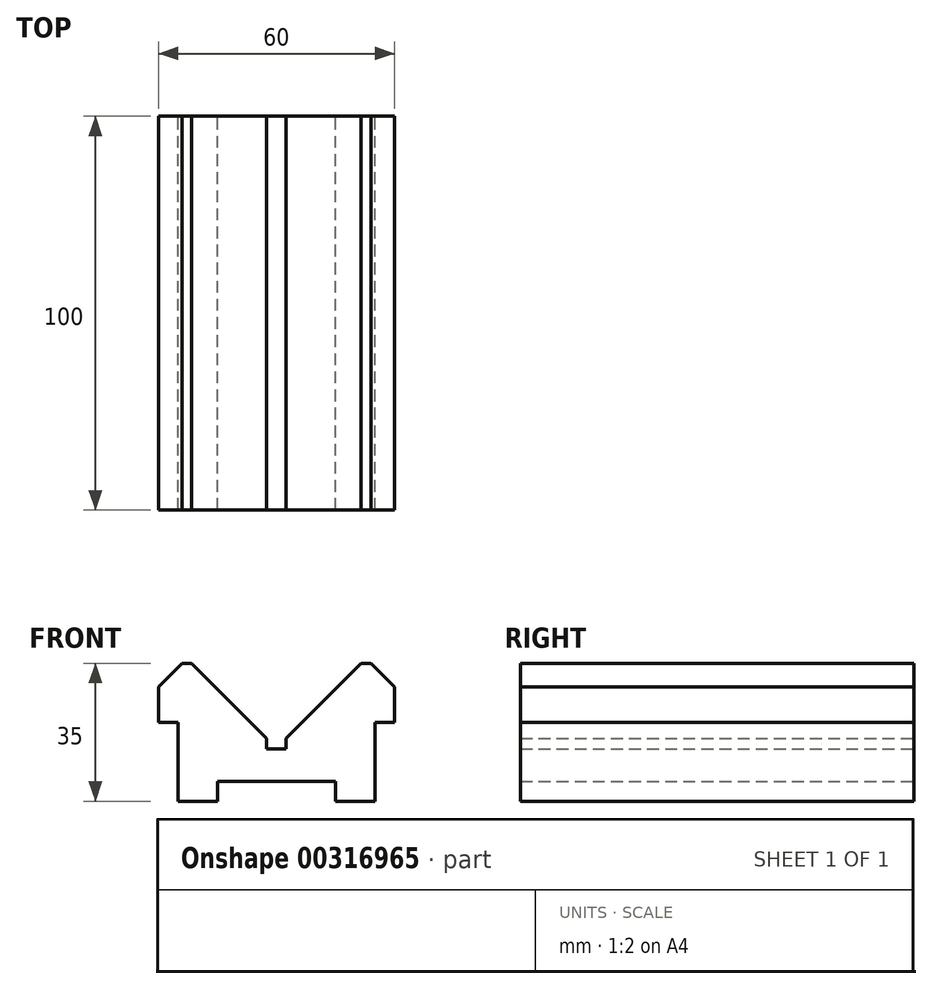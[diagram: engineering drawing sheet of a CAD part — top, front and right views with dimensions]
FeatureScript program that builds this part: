
annotation { "Feature Type Name" : "Feature", "Feature Type Description" : "" }
export const myFeature = defineFeature(function(context is Context, id is Id, definition is map)
    precondition{}
    {
        {
            var Q0;
            Q0=qCreatedBy(makeId("Front.planeOp"),FACE);
            var sketch = newSketch(context, id + "F0", { "sketchPlane" : qUnion([Q0])});
            skLineSegment(sketch, "E0", {"start": v(0, 0) * mm, "end": v(-21.5, 0) * mm, "construction": true});
            skLineSegment(sketch, "E1", {"start": v(0, -30) * mm, "end": v(-15, -30) * mm});
            skLineSegment(sketch, "E2.MirrorCS", {"start": v(0, -30) * mm, "end": v(15, -30) * mm});
            skLineSegment(sketch, "E3", {"start": v(15, -30) * mm, "end": v(15, -35) * mm});
            skLineSegment(sketch, "E4", {"start": v(0, -21.78) * mm, "end": v(2.5, -21.78) * mm});
            skLineSegment(sketch, "E5", {"start": v(15, -35) * mm, "end": v(25, -35) * mm});
            skLineSegment(sketch, "E6", {"start": v(25, -35) * mm, "end": v(25, -15) * mm});
            skLineSegment(sketch, "E7", {"start": v(25, -15) * mm, "end": v(30, -15) * mm});
            skLineSegment(sketch, "E8.MirrorCS", {"start": v(0, 0) * mm, "end": v(21.5, 0) * mm, "construction": true});
            skLineSegment(sketch, "E9", {"start": v(30, 0) * mm, "end": v(24, 0) * mm});
            skLineSegment(sketch, "E10", {"start": v(24, 0) * mm, "end": v(30, -6) * mm});
            skLineSegment(sketch, "E11", {"start": v(30, -6) * mm, "end": v(30, -15) * mm});
            skLineSegment(sketch, "E12", {"start": v(24, 0) * mm, "end": v(21.5, 0) * mm});
            skLineSegment(sketch, "E13", {"start": v(21.5, 0) * mm, "end": v(2.5, -19) * mm});
            skLineSegment(sketch, "E14", {"start": v(2.5, -19) * mm, "end": v(2.5, -21.78) * mm});
            skLineSegment(sketch, "E15", {"start": v(0, -21.78) * mm, "end": v(-2.5, -21.78) * mm});
            skLineSegment(sketch, "E16.MirrorCS", {"start": v(-21.5, 0) * mm, "end": v(-2.5, -19) * mm});
            skLineSegment(sketch, "E17.MirrorCS", {"start": v(-2.5, -19) * mm, "end": v(-2.5, -21.78) * mm});
            skLineSegment(sketch, "E18.MirrorCS", {"start": v(-24, 0) * mm, "end": v(-30, -6) * mm});
            skLineSegment(sketch, "E19.MirrorCS", {"start": v(-24, 0) * mm, "end": v(-21.5, 0) * mm});
            skLineSegment(sketch, "E20.MirrorCS", {"start": v(-25, -35) * mm, "end": v(-25, -15) * mm});
            skLineSegment(sketch, "E21.MirrorCS", {"start": v(-25, -15) * mm, "end": v(-30, -15) * mm});
            skLineSegment(sketch, "E22.MirrorCS", {"start": v(-15, -35) * mm, "end": v(-25, -35) * mm});
            skLineSegment(sketch, "E23.MirrorCS", {"start": v(-15, -30) * mm, "end": v(-15, -35) * mm});
            skLineSegment(sketch, "E24.MirrorCS", {"start": v(-30, -6) * mm, "end": v(-30, -15) * mm});
            skSolve(sketch);
        }
        {
            var Q0;
            Q0=makeQuery(id+"F0.imprint","IMPRINT",FACE,{"disambiguationData":[TD([[makeQuery(id+"F0.imprint","IMPRINT",EDGE,{"derivedFrom":sQuery(id+"F0.wireOp",EDGE,"E1")}),-1.0]])]});
            extrude(context, id + "F1", {"entities" : qUnion([Q0]), "depth" : 100 * mm});
        }
    });
